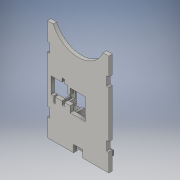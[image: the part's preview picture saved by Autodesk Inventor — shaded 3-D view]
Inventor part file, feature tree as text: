
AUTODESK INVENTOR PART (.ipt)
format: ipt  version: 2016 (Build 200138000, 138)  size: 430,592 bytes
history: native  units: in
note: dims shown in document units (in); Inventor stores cm internally (conversion verified against a paired STEP export)
features: reference x25, extrude x18, sketch x17, plane x1, projected_geometry x1
ambient origin geometry x8: Origin, YZ Plane, XZ Plane, XY Plane, X Axis, Y Axis, Z Axis, Center Point
bodies: Solid1 (feature_tree)
feature tree (62):
  extrude  "Extrusion1"  Depth=0.1969in TaperAngle=0.0deg
  extrude  "Extrusion2"  Depth=0.1969in TaperAngle=0.0deg
  extrude  "Extrusion3"  Depth=0.0787in
  extrude  "Extrusion4"  Depth=0.1969in TaperAngle=0.0deg
  extrude  "Extrusion6"  Depth=0.1969in
  extrude  "Extrusion7"  Depth=0.1969in TaperAngle=0.0deg
  extrude  "Extrusion8"  Depth=0.5in
  extrude  "Extrusion9"  Depth=0.4in TaperAngle=0.0deg
  extrude  "Extrusion10"  Depth=0.15in
  plane  "Work Plane1"
  extrude  "Extrusion11"  Depth=0.1181in
  extrude  "Extrusion12"  Depth=1.0in TaperAngle=0.0deg
  extrude  "Extrusion13"  Depth=0.325in
  extrude  "Extrusion14"  Depth=0.0197in
  extrude  "Extrusion15"  Depth=0.0787in
  extrude  "Extrusion16"  Depth=0.0787in
  extrude  "Extrusion17"  Depth=0.079in TaperAngle=0.0deg
  extrude  "Extrusion18"  Depth=0.0197in
  extrude  "Extrusion19"  Depth=0.0197in
  sketch  "Sketch1"  dims[d0=6.0in d1=0.1969in d2=0.0in]
  sketch  "Sketch2"  dims[d3=0.5906in d4=0.1969in d5=0.0in]
  reference  "Reference2"
  reference  "Reference3"
  sketch  "Sketch4"  dims[d6=3.0in d7=0.0787in]
  sketch  "Sketch6"  dims[d8=0.0787in d9=0.1969in d10=0.0in]
  sketch  "Sketch7"  dims[d11=0.1969in d12=0.1969in]
  sketch  "Sketch8"  dims[d13=0.1969in d14=0.1969in d15=0.0in]
  reference  "Reference6"
  reference  "Reference7"
  reference  "Reference8"
  reference  "Reference9"
  reference  "Reference10"
  reference  "Reference11"
  reference  "Reference12"
  reference  "Reference13"
  reference  "Reference14"
  reference  "Reference15"
  sketch  "Sketch9"  dims[d18=0.25in d19=0.5in]
  sketch  "Sketch10"  dims[d20=0.4in d21=0.0in d24=0.25in d25=0.0in]
  sketch  "Sketch11"  dims[d26=0.15in d27=0.1378in]
  reference  "Reference16"
  reference  "Reference17"
  sketch  "Sketch12"  dims[d28=0.0394in d29=0.1181in]
  projected_geometry  "Projected Loop1"
  sketch  "Sketch13"  dims[d30=0.0394in d31=1.0in d32=0.0in]
  reference  "Reference18"
  reference  "Reference19"
  reference  "Reference20"
  reference  "Reference21"
  reference  "Reference22"
  sketch  "Sketch14"  dims[d33=0.02in d34=0.325in]
  reference  "Reference23"
  sketch  "Sketch15"  dims[d35=0.02in d36=0.0197in]
  reference  "Reference24"
  reference  "Reference25"
  reference  "Reference26"
  sketch  "Sketch16"  dims[d37=0.0197in d38=0.0787in]
  reference  "Reference27"
  sketch  "Sketch17"  dims[d39=0.0197in d40=0.0787in]
  reference  "Reference28"
  sketch  "Sketch18"  dims[d41=0.303in d42=0.0in d43=0.079in d44=0.0in]
  sketch  "Sketch20"  dims[d45=0.0197in d46=0.0197in d47=0.0197in d48=0.0984in d49=0.0984in d50=0.1984in d51=0.0in d52=0.3937in d53=0.0in d54=0.0197in d55=0.0197in d56=0.0787in d57=0.0197in d58=0.0197in d59=0.0787in d60=0.0787in d61=0.4724in d62=0.0in d63=0.297in d64=0.0in d65=0.1969in d66=0.1969in d67=0.1181in d68=0.1181in d69=0.6299in d70=0.0in d71=0.5047in d72=0.0in d73=0.1181in d74=0.1575in d75=0.0098in d76=0.0787in d77=0.0787in d78=0.0098in d79=0.0098in d80=0.0787in d81=0.3937in d82=0.0in d83=1.0in d84=0.5in d85=0.118in d86=1.0in d87=0.5in d88=0.118in d89=0.3937in d90=0.0in d91=0.8226in d92=0.0in]
